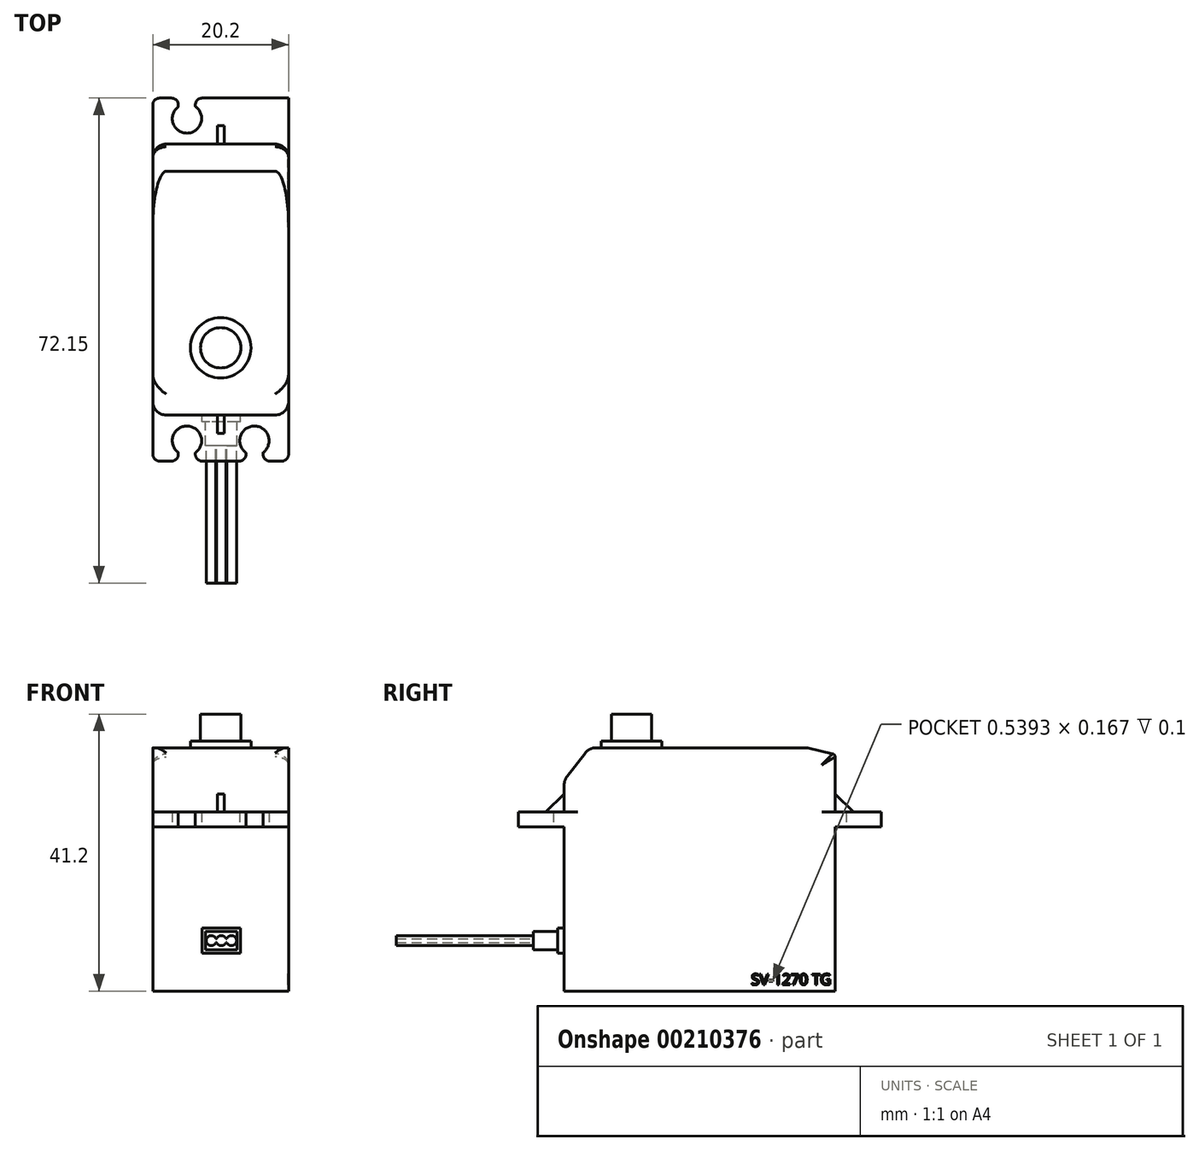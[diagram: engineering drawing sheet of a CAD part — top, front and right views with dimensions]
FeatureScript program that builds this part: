
annotation { "Feature Type Name" : "Feature", "Feature Type Description" : "" }
export const myFeature = defineFeature(function(context is Context, id is Id, definition is map)
    precondition{}
    {
        {
            var Q0;
            Q0=qCreatedBy(makeId("Right.planeOp"),FACE);
            var sketch = newSketch(context, id + "F0", { "sketchPlane" : qUnion([Q0])});
            skLineSegment(sketch, "E0.bottom", {"start": v(-15.65, 18.6) * mm, "end": v(12, 18.6) * mm});
            skLineSegment(sketch, "E0.top", {"start": v(-20.15, -18.6) * mm, "end": v(20.15, -18.6) * mm});
            skLineSegment(sketch, "E0.left", {"start": v(-20.15, 12.78) * mm, "end": v(-20.15, 8.05) * mm});
            skLineSegment(sketch, "E0.right", {"start": v(20.15, 16.61) * mm, "end": v(20.15, 8.05) * mm});
            skPoint(sketch, "E0.middle", {"position": v(0, 0) * mm});
            skLineSegment(sketch, "E1", {"start": v(0, -43.02) * mm, "end": v(0, 43.44) * mm, "construction": true});
            skPoint(sketch, "E1.startSnap0", {"position": v(0, 18.6) * mm});
            skLineSegment(sketch, "E2.0", {"start": v(27, -43.02) * mm, "end": v(27, 43.44) * mm, "construction": true});
            skLineSegment(sketch, "E3.0", {"start": v(-27, -43.02) * mm, "end": v(-27, 43.44) * mm, "construction": true});
            skLineSegment(sketch, "E4", {"start": v(-27, 5.8) * mm, "end": v(27, 5.8) * mm});
            skLineSegment(sketch, "E5.0", {"start": v(-27, 8.05) * mm, "end": v(27, 8.05) * mm});
            skLineSegment(sketch, "E6.0", {"start": v(12, 18.6) * mm, "end": v(12, -18.6) * mm, "construction": true});
            skLineSegment(sketch, "E7.0", {"start": v(-15.65, 18.6) * mm, "end": v(-15.65, -18.6) * mm, "construction": true});
            skLineSegment(sketch, "E8", {"start": v(-15.65, 18.6) * mm, "end": v(-20.15, 12.78) * mm});
            skLineSegment(sketch, "E9", {"start": v(12, 18.6) * mm, "end": v(20.15, 16.61) * mm});
            skPoint(sketch, "E10.orphan", {"position": v(-20.15, 18.6) * mm});
            skPoint(sketch, "E11.orphan", {"position": v(20.15, 18.6) * mm});
            skLineSegment(sketch, "E12", {"start": v(-20.15, 10.7) * mm, "end": v(-22.9, 8.05) * mm});
            skLineSegment(sketch, "E13", {"start": v(-20.15, 10.7) * mm, "end": v(20.15, 10.7) * mm, "construction": true});
            skLineSegment(sketch, "E14.0", {"start": v(22.9, -43.02) * mm, "end": v(22.9, 43.44) * mm, "construction": true});
            skLineSegment(sketch, "E15", {"start": v(20.15, 10.7) * mm, "end": v(22.9, 8.05) * mm});
            skLineSegment(sketch, "E16.trimOffspring", {"start": v(-20.15, 5.8) * mm, "end": v(-20.15, -18.6) * mm});
            skLineSegment(sketch, "E17.trimOffspring", {"start": v(20.15, 5.8) * mm, "end": v(20.15, -18.6) * mm});
            skLineSegment(sketch, "E18", {"start": v(-27, 8.05) * mm, "end": v(-27, 5.8) * mm});
            skLineSegment(sketch, "E19", {"start": v(27, 8.05) * mm, "end": v(27, 5.8) * mm});
            skSolve(sketch);
        }
        {
            var Q0;
            Q0=makeQuery(id+"F0.imprint","IMPRINT",FACE,{"disambiguationData":[TD([[makeQuery(id+"F0.imprint","IMPRINT",EDGE,{"derivedFrom":sQuery(id+"F0.wireOp",EDGE,"E0.top")}),1.0]])]});
            var Q1;
            {var subQ0=sQuery(id+"F0.wireOp",EDGE,"E18");Q1=makeQuery(id+"F0.imprint","IMPRINT",FACE,{"disambiguationData":[TD([[makeQuery(id+"F0.imprint","IMPRINT",EDGE,{"derivedFrom":subQ0}),1.0]])]});}
            var Q2;
            Q2=makeQuery(id+"F0.imprint","IMPRINT",FACE,{"disambiguationData":[TD([[makeQuery(id+"F0.imprint","IMPRINT",EDGE,{"derivedFrom":sQuery(id+"F0.wireOp",EDGE,"E0.bottom")}),-1.0]])]});
            extrude(context, id + "F1", {"entities" : qUnion([Q0, Q1, Q2]), "endBound" : BoundingType.SYMMETRIC, "depth" : 20.2 * mm});
        }
        {
            var Q0;
            {var subQ3=sQuery(id+"F0.wireOp",EDGE,"E12");Q0=makeQuery(id+"F0.imprint","IMPRINT",FACE,{"disambiguationData":[TD([[makeQuery(id+"F0.imprint","IMPRINT",EDGE,{"derivedFrom":subQ3}),1.0]])]});}
            var Q1;
            {var subQ3=sQuery(id+"F0.wireOp",EDGE,"E15");Q1=makeQuery(id+"F0.imprint","IMPRINT",FACE,{"disambiguationData":[TD([[makeQuery(id+"F0.imprint","IMPRINT",EDGE,{"derivedFrom":subQ3}),-1.0]])]});}
            extrude(context, id + "F2", {"entities" : qUnion([Q0, Q1]), "operationType" : NewBodyOperationType.ADD, "endBound" : BoundingType.SYMMETRIC, "depth" : 1 * mm});
        }
        {
            var Q0;
            Q0=makeQuery(id+"F1.opExtrude","SWEPT_FACE",FACE,{"disambiguationData":[OSD([sQuery(id+"F0.wireOp",EDGE,"E0.bottom")])]});
            var sketch = newSketch(context, id + "F3", { "sketchPlane" : qUnion([Q0])});
            skLineSegment(sketch, "E20.0", {"start": v(10.1, -18.65) * mm, "end": v(10.1, 17) * mm});
            skLineSegment(sketch, "E21.0", {"start": v(-10.1, -18.65) * mm, "end": v(-10.1, 17) * mm});
            skLineSegment(sketch, "E22.0", {"start": v(10.1, -14.65) * mm, "end": v(-10.1, -14.65) * mm, "construction": true});
            skLineSegment(sketch, "E23", {"start": v(0, 0) * mm, "end": v(0, -15.65) * mm, "construction": true});
            skCircle(sketch, "E24", {"center": v(0, -10.15) * mm, "radius": 4.5 * mm});
            skCircle(sketch, "E25", {"center": v(0, -10.15) * mm, "radius": 3 * mm});
            skLineSegment(sketch, "E26.0", {"start": v(10.1, -18.65) * mm, "end": v(-10.1, -18.65) * mm});
            skPoint(sketch, "E27.orphan", {"position": v(10.1, -15.65) * mm});
            skPoint(sketch, "E28.orphan", {"position": v(-10.1, -15.65) * mm});
            skLineSegment(sketch, "E29.0", {"start": v(10.1, 17) * mm, "end": v(-10.1, 17) * mm});
            skPoint(sketch, "E30.orphan", {"position": v(10.1, 12) * mm});
            skPoint(sketch, "E31.orphan", {"position": v(-10.1, 12) * mm});
            skSolve(sketch);
        }
        {
            var Q0;
            Q0=makeQuery(id+"F3.imprint","IMPRINT",FACE,{"disambiguationData":[TD([[makeQuery(id+"F3.imprint","IMPRINT",EDGE,{"derivedFrom":sQuery(id+"F3.wireOp",EDGE,"E24")}),-1.0]])]});
            var Q1;
            {var subQ2=sQuery(id+"F3.wireOp",EDGE,"E29.0");Q1=makeQuery(id+"F3.imprint","IMPRINT",FACE,{"disambiguationData":[TD([[makeQuery(id+"F3.imprint","IMPRINT",EDGE,{"derivedFrom":subQ2}),1.0]])]});}
            var Q2;
            {var subQ2=sQuery(id+"F3.wireOp",EDGE,"E26.0");Q2=makeQuery(id+"F3.imprint","IMPRINT",FACE,{"disambiguationData":[TD([[makeQuery(id+"F3.imprint","IMPRINT",EDGE,{"derivedFrom":subQ2}),-1.0]])]});}
            extrude(context, id + "F4", {"entities" : qUnion([Q0, Q1, Q2]), "operationType" : NewBodyOperationType.REMOVE, "oppositeDirection" : true, "depth" : 1 * mm});
        }
        {
            var Q0;
            Q0=makeQuery(id+"F3.imprint","IMPRINT",FACE,{"disambiguationData":[TD([[makeQuery(id+"F3.imprint","IMPRINT",EDGE,{"derivedFrom":sQuery(id+"F3.wireOp",EDGE,"E25")}),1.0]])]});
            extrude(context, id + "F5", {"entities" : qUnion([Q0]), "operationType" : NewBodyOperationType.ADD, "depth" : 4 * mm});
        }
        {
            var Q0;
            Q0=qCreatedBy(makeId("Top.planeOp"),FACE);
            var sketch = newSketch(context, id + "F6", { "sketchPlane" : qUnion([Q0])});
            skLineSegment(sketch, "E32.0", {"start": v(10.1, -24) * mm, "end": v(-10.1, -24) * mm, "construction": true});
            skPoint(sketch, "E33.newPointB", {"position": v(10.1, -27) * mm});
            skLineSegment(sketch, "E34", {"start": v(0, -27.5) * mm, "end": v(0, -27) * mm});
            skLineSegment(sketch, "E35.MirrorCS", {"start": v(3.77, -26) * mm, "end": v(3.77, -25.8) * mm});
            skLineSegment(sketch, "E36.MirrorCS", {"start": v(10.02, -26) * mm, "end": v(10.38, -26) * mm});
            skLineSegment(sketch, "E37.MirrorCS", {"start": v(6.3, -26) * mm, "end": v(6.3, -25.78) * mm});
            skLineSegment(sketch, "E38.MirrorCS", {"start": v(7.3, -27) * mm, "end": v(9.1, -27) * mm});
            skLineSegment(sketch, "E39.MirrorCS", {"start": v(9.1, -27) * mm, "end": v(7.3, -27) * mm});
            skArc(sketch, "E40.MirrorCS", {"start": v(10.1, -26) * mm, "mid": v(9.8, -26.7) * mm, "end": v(9.1, -27) * mm});
            skArc(sketch, "E41.MirrorCS", {"start": v(7.3, -27) * mm, "mid": v(6.6, -26.7) * mm, "end": v(6.3, -26) * mm});
            skLineSegment(sketch, "E42.MirrorCS", {"start": v(10.38, -26) * mm, "end": v(10.38, -27.5) * mm});
            skLineSegment(sketch, "E43.MirrorCS", {"start": v(0, -27) * mm, "end": v(2.77, -27) * mm});
            skArc(sketch, "E44.MirrorCS", {"start": v(3.77, -26) * mm, "mid": v(3.47, -26.7) * mm, "end": v(2.77, -27) * mm});
            skLineSegment(sketch, "E45.MirrorCS", {"start": v(10.38, -27.5) * mm, "end": v(0, -27.5) * mm});
            skPoint(sketch, "E46.MirrorP", {"position": v(3.77, -27) * mm});
            skArc(sketch, "E47", {"start": v(6.34, -25.7) * mm, "mid": v(5, -21.79) * mm, "end": v(3.73, -25.72) * mm});
            skPoint(sketch, "E48.orphan", {"position": v(6.3, -25.52) * mm});
            skPoint(sketch, "E49.orphan", {"position": v(3.77, -25.56) * mm});
            skPoint(sketch, "E50.visualSharp", {"position": v(6.3, -25.73) * mm});
            skArc(sketch, "E50.filletArc", {"start": v(6.34, -25.7) * mm, "mid": v(6.31, -25.73) * mm, "end": v(6.3, -25.78) * mm});
            skPoint(sketch, "E51.visualSharp", {"position": v(3.77, -25.75) * mm});
            skArc(sketch, "E51.filletArc", {"start": v(3.77, -25.8) * mm, "mid": v(3.76, -25.76) * mm, "end": v(3.73, -25.72) * mm});
            skArc(sketch, "E52.MirrorCS", {"start": v(-3.77, -25.8) * mm, "mid": v(-3.76, -25.76) * mm, "end": v(-3.73, -25.72) * mm});
            skLineSegment(sketch, "E53.MirrorCS", {"start": v(-3.77, -26) * mm, "end": v(-3.77, -25.8) * mm});
            skArc(sketch, "E54.MirrorCS", {"start": v(-6.34, -25.7) * mm, "mid": v(-6.31, -25.73) * mm, "end": v(-6.3, -25.78) * mm});
            skLineSegment(sketch, "E55.MirrorCS", {"start": v(-6.3, -26) * mm, "end": v(-6.3, -25.78) * mm});
            skLineSegment(sketch, "E56.MirrorCS", {"start": v(-10.02, -26) * mm, "end": v(-10.38, -26) * mm});
            skLineSegment(sketch, "E57.MirrorCS", {"start": v(-10.38, -26) * mm, "end": v(-10.38, -27.5) * mm});
            skLineSegment(sketch, "E58.MirrorCS", {"start": v(-9.1, -27) * mm, "end": v(-7.3, -27) * mm});
            skArc(sketch, "E59.MirrorCS", {"start": v(-10.1, -26) * mm, "mid": v(-9.8, -26.7) * mm, "end": v(-9.1, -27) * mm});
            skPoint(sketch, "E60.MirrorP", {"position": v(-10.1, -27) * mm});
            skArc(sketch, "E61.MirrorCS", {"start": v(-3.77, -26) * mm, "mid": v(-3.47, -26.7) * mm, "end": v(-2.77, -27) * mm});
            skLineSegment(sketch, "E62.MirrorCS", {"start": v(-7.3, -27) * mm, "end": v(-9.1, -27) * mm});
            skLineSegment(sketch, "E63.MirrorCS", {"start": v(0, -27) * mm, "end": v(-2.77, -27) * mm});
            skArc(sketch, "E64.MirrorCS", {"start": v(-7.3, -27) * mm, "mid": v(-6.6, -26.7) * mm, "end": v(-6.3, -26) * mm});
            skPoint(sketch, "E65.MirrorP", {"position": v(-3.77, -25.75) * mm});
            skPoint(sketch, "E66.MirrorP", {"position": v(-3.77, -25.56) * mm});
            skPoint(sketch, "E67.MirrorP", {"position": v(-3.77, -27) * mm});
            skLineSegment(sketch, "E68.MirrorCS", {"start": v(-10.38, -27.5) * mm, "end": v(0, -27.5) * mm});
            skArc(sketch, "E69.MirrorCS", {"start": v(-6.34, -25.7) * mm, "mid": v(-5, -21.79) * mm, "end": v(-3.73, -25.72) * mm});
            skPoint(sketch, "E70.MirrorP", {"position": v(-6.3, -25.73) * mm});
            skPoint(sketch, "E71.MirrorP", {"position": v(-6.3, -25.52) * mm});
            skLineSegment(sketch, "E72.MirrorCS", {"start": v(-10.1, -24) * mm, "end": v(10.1, -24) * mm, "construction": true});
            skLineSegment(sketch, "E73.MirrorCS", {"start": v(0, 27.5) * mm, "end": v(0, 27) * mm});
            skArc(sketch, "E74.MirrorCS", {"start": v(-3.77, 25.8) * mm, "mid": v(-3.76, 25.76) * mm, "end": v(-3.73, 25.72) * mm});
            skLineSegment(sketch, "E75.MirrorCS", {"start": v(-3.77, 26) * mm, "end": v(-3.77, 25.8) * mm});
            skArc(sketch, "E76.MirrorCS", {"start": v(3.77, 25.8) * mm, "mid": v(3.76, 25.76) * mm, "end": v(3.73, 25.72) * mm});
            skLineSegment(sketch, "E77.MirrorCS", {"start": v(3.77, 26) * mm, "end": v(3.77, 25.8) * mm});
            skLineSegment(sketch, "E78.MirrorCS", {"start": v(6.3, 26) * mm, "end": v(6.3, 25.78) * mm});
            skArc(sketch, "E79.MirrorCS", {"start": v(6.34, 25.7) * mm, "mid": v(6.31, 25.73) * mm, "end": v(6.3, 25.78) * mm});
            skArc(sketch, "E80.MirrorCS", {"start": v(-6.34, 25.7) * mm, "mid": v(-6.31, 25.73) * mm, "end": v(-6.3, 25.78) * mm});
            skLineSegment(sketch, "E81.MirrorCS", {"start": v(-6.3, 26) * mm, "end": v(-6.3, 25.78) * mm});
            skArc(sketch, "E82.MirrorCS", {"start": v(-10.1, 26) * mm, "mid": v(-9.8, 26.7) * mm, "end": v(-9.1, 27) * mm});
            skLineSegment(sketch, "E83.MirrorCS", {"start": v(7.3, 27) * mm, "end": v(9.1, 27) * mm});
            skLineSegment(sketch, "E84.MirrorCS", {"start": v(-7.3, 27) * mm, "end": v(-9.1, 27) * mm});
            skLineSegment(sketch, "E85.MirrorCS", {"start": v(-10.38, 26) * mm, "end": v(-10.38, 27.5) * mm});
            skLineSegment(sketch, "E86.MirrorCS", {"start": v(10.38, 26) * mm, "end": v(10.38, 27.5) * mm});
            skLineSegment(sketch, "E87.MirrorCS", {"start": v(10.02, 26) * mm, "end": v(10.38, 26) * mm});
            skLineSegment(sketch, "E88.MirrorCS", {"start": v(-10.02, 26) * mm, "end": v(-10.38, 26) * mm});
            skArc(sketch, "E89.MirrorCS", {"start": v(10.1, 26) * mm, "mid": v(9.8, 26.7) * mm, "end": v(9.1, 27) * mm});
            skLineSegment(sketch, "E90.MirrorCS", {"start": v(-9.1, 27) * mm, "end": v(-7.3, 27) * mm});
            skLineSegment(sketch, "E91.MirrorCS", {"start": v(9.1, 27) * mm, "end": v(7.3, 27) * mm});
            skPoint(sketch, "E92.MirrorP", {"position": v(3.77, 25.75) * mm});
            skPoint(sketch, "E93.MirrorP", {"position": v(10.1, 27) * mm});
            skArc(sketch, "E94.MirrorCS", {"start": v(-3.77, 26) * mm, "mid": v(-3.47, 26.7) * mm, "end": v(-2.77, 27) * mm});
            skPoint(sketch, "E95.MirrorP", {"position": v(-10.1, 27) * mm});
            skArc(sketch, "E96.MirrorCS", {"start": v(3.77, 26) * mm, "mid": v(3.47, 26.7) * mm, "end": v(2.77, 27) * mm});
            skPoint(sketch, "E97.MirrorP", {"position": v(6.3, 25.73) * mm});
            skPoint(sketch, "E98.MirrorP", {"position": v(-3.77, 25.75) * mm});
            skPoint(sketch, "E99.MirrorP", {"position": v(6.3, 25.52) * mm});
            skLineSegment(sketch, "E100.MirrorCS", {"start": v(10.1, 24) * mm, "end": v(-10.1, 24) * mm, "construction": true});
            skLineSegment(sketch, "E101.MirrorCS", {"start": v(-10.1, 24) * mm, "end": v(10.1, 24) * mm, "construction": true});
            skPoint(sketch, "E102.MirrorP", {"position": v(-3.77, 25.56) * mm});
            skPoint(sketch, "E103.MirrorP", {"position": v(3.77, 25.56) * mm});
            skPoint(sketch, "E104.MirrorP", {"position": v(-6.3, 25.73) * mm});
            skLineSegment(sketch, "E105.MirrorCS", {"start": v(0, 27) * mm, "end": v(2.77, 27) * mm});
            skPoint(sketch, "E106.MirrorP", {"position": v(-6.3, 25.52) * mm});
            skPoint(sketch, "E107.MirrorP", {"position": v(-3.77, 27) * mm});
            skArc(sketch, "E108.MirrorCS", {"start": v(6.34, 25.7) * mm, "mid": v(5, 21.79) * mm, "end": v(3.73, 25.72) * mm});
            skPoint(sketch, "E109.MirrorP", {"position": v(3.77, 27) * mm});
            skLineSegment(sketch, "E110.MirrorCS", {"start": v(0, 27) * mm, "end": v(-2.77, 27) * mm});
            skArc(sketch, "E111.MirrorCS", {"start": v(-6.34, 25.7) * mm, "mid": v(-5, 21.79) * mm, "end": v(-3.73, 25.72) * mm});
            skLineSegment(sketch, "E112.MirrorCS", {"start": v(10.38, 27.5) * mm, "end": v(0, 27.5) * mm});
            skArc(sketch, "E113.MirrorCS", {"start": v(7.3, 27) * mm, "mid": v(6.6, 26.7) * mm, "end": v(6.3, 26) * mm});
            skArc(sketch, "E114.MirrorCS", {"start": v(-7.3, 27) * mm, "mid": v(-6.6, 26.7) * mm, "end": v(-6.3, 26) * mm});
            skLineSegment(sketch, "E115.MirrorCS", {"start": v(-10.38, 27.5) * mm, "end": v(0, 27.5) * mm});
            skSolve(sketch);
        }
        {
            var Q0;
            Q0=makeQuery(id+"F6.imprint","IMPRINT",FACE,{"disambiguationData":[TD([[makeQuery(id+"F6.imprint","IMPRINT",EDGE,{"derivedFrom":sQuery(id+"F6.wireOp",EDGE,"E35.MirrorCS")}),-1.0]])]});
            var Q1;
            Q1=makeQuery(id+"F6.imprint","IMPRINT",FACE,{"disambiguationData":[TD([[makeQuery(id+"F6.imprint","IMPRINT",EDGE,{"derivedFrom":sQuery(id+"F6.wireOp",EDGE,"E55.MirrorCS")}),-1.0]])]});
            var Q2;
            Q2=makeQuery(id+"F6.imprint","IMPRINT",FACE,{"disambiguationData":[TD([[makeQuery(id+"F6.imprint","IMPRINT",EDGE,{"derivedFrom":sQuery(id+"F6.wireOp",EDGE,"E76.MirrorCS")}),1.0]])]});
            var Q3;
            Q3=makeQuery(id+"F6.imprint","IMPRINT",FACE,{"disambiguationData":[TD([[makeQuery(id+"F6.imprint","IMPRINT",EDGE,{"derivedFrom":sQuery(id+"F6.wireOp",EDGE,"E74.MirrorCS")}),-1.0]])]});
            extrude(context, id + "F7", {"entities" : qUnion([Q0, Q1, Q2, Q3]), "operationType" : NewBodyOperationType.REMOVE, "depth" : 25 * mm});
        }
        {
            var Q0;
            Q0=makeQuery(id+"F1.opExtrude","CAP_EDGE",EDGE,{"disambiguationData":[OSD([sQuery(id+"F0.wireOp",EDGE,"E0.right")])],"isStart":true});
            var Q1;
            Q1=makeQuery(id+"F1.opExtrude","CAP_EDGE",EDGE,{"disambiguationData":[OSD([sQuery(id+"F0.wireOp",EDGE,"E9")])],"isStart":true});
            var Q2;
            Q2=makeQuery(id+"F4.boolean.opBoolean","COPY",EDGE,{"derivedFrom":makeQuery(id+"F4.opExtrude","CAP_EDGE",EDGE,{"disambiguationData":[OSD([sQuery(id+"F3.wireOp",EDGE,"E21.0")])],"isStart":false})});
            var Q3;
            Q3=makeQuery(id+"F1.opExtrude","CAP_EDGE",EDGE,{"disambiguationData":[OSD([sQuery(id+"F0.wireOp",EDGE,"E8")])],"isStart":true});
            var Q4;
            Q4=makeQuery(id+"F1.opExtrude","CAP_EDGE",EDGE,{"disambiguationData":[OSD([sQuery(id+"F0.wireOp",EDGE,"E0.left")])],"isStart":true});
            var Q5;
            Q5=makeQuery(id+"F1.opExtrude","CAP_EDGE",EDGE,{"disambiguationData":[OSD([sQuery(id+"F0.wireOp",EDGE,"E0.right")])],"isStart":false});
            var Q6;
            Q6=makeQuery(id+"F1.opExtrude","CAP_EDGE",EDGE,{"disambiguationData":[OSD([sQuery(id+"F0.wireOp",EDGE,"E9")])],"isStart":false});
            var Q7;
            Q7=makeQuery(id+"F4.boolean.opBoolean","COPY",EDGE,{"derivedFrom":makeQuery(id+"F4.opExtrude","CAP_EDGE",EDGE,{"disambiguationData":[OSD([sQuery(id+"F3.wireOp",EDGE,"E20.0")])],"isStart":false})});
            var Q8;
            Q8=makeQuery(id+"F1.opExtrude","SWEPT_EDGE",EDGE,{"disambiguationData":[OSD([sQuery(id+"F0.wireOp",EDGE,"E0.left"),sQuery(id+"F0.wireOp",EDGE,"E8")])]});
            var Q9;
            Q9=makeQuery(id+"F4.boolean.opBoolean","INTERSECT",EDGE,{"derivedFrom":[makeQuery(id+"F1.opExtrude","SWEPT_FACE",FACE,{"disambiguationData":[OSD([sQuery(id+"F0.wireOp",EDGE,"E8")])]}),makeQuery(id+"F4.opExtrude","CAP_FACE",FACE,{"disambiguationData":[OSD([sQuery(id+"F3.wireOp",EDGE,"E20.0"),sQuery(id+"F3.wireOp",EDGE,"E21.0"),sQuery(id+"F3.wireOp",EDGE,"E24"),sQuery(id+"F3.wireOp",EDGE,"E26.0"),sQuery(id+"F3.wireOp",EDGE,"E29.0")])],"isStart":false})]});
            var Q10;
            Q10=makeQuery(id+"F1.opExtrude","CAP_EDGE",EDGE,{"disambiguationData":[OSD([sQuery(id+"F0.wireOp",EDGE,"E0.left")])],"isStart":false});
            var Q11;
            Q11=makeQuery(id+"F1.opExtrude","CAP_EDGE",EDGE,{"disambiguationData":[OSD([sQuery(id+"F0.wireOp",EDGE,"E8")])],"isStart":false});
            fillet(context, id + "F8", {"entities" : qUnion([Q0, Q1, Q2, Q3, Q4, Q5, Q6, Q7, Q8, Q9, Q10, Q11]), "radius" : 2 * mm, "tangentPropagation" : true, "allowEdgeOverflow" : false});
        }
        {
            var Q0;
            Q0=makeQuery(id+"F1.opExtrude","SWEPT_FACE",FACE,{"disambiguationData":[OSD([sQuery(id+"F0.wireOp",EDGE,"E16.trimOffspring")])]});
            var sketch = newSketch(context, id + "F9", { "sketchPlane" : qUnion([Q0])});
            skLineSegment(sketch, "E116.0", {"start": v(2.97, -12.95) * mm, "end": v(-2.77, -12.95) * mm});
            skLineSegment(sketch, "E117.0", {"start": v(2.97, -9.25) * mm, "end": v(-2.77, -9.25) * mm});
            skLineSegment(sketch, "E118", {"start": v(2.97, -9.25) * mm, "end": v(2.97, -12.95) * mm});
            skLineSegment(sketch, "E119", {"start": v(-2.77, -9.25) * mm, "end": v(-2.77, -12.95) * mm});
            skLineSegment(sketch, "E120.0", {"start": v(2.47, -9.75) * mm, "end": v(-2.27, -9.75) * mm});
            skLineSegment(sketch, "E120.1", {"start": v(2.47, -9.75) * mm, "end": v(2.47, -12.45) * mm});
            skLineSegment(sketch, "E120.2", {"start": v(2.47, -12.45) * mm, "end": v(-2.27, -12.45) * mm});
            skLineSegment(sketch, "E120.3", {"start": v(-2.27, -9.75) * mm, "end": v(-2.27, -12.45) * mm});
            skLineSegment(sketch, "E121", {"start": v(2.47, -11.1) * mm, "end": v(-2.27, -11.1) * mm, "construction": true});
            skArc(sketch, "E122", {"start": v(-0.59, -11.4) * mm, "mid": v(0.1, -11.85) * mm, "end": v(0.79, -11.4) * mm});
            skArc(sketch, "E123", {"start": v(-0.71, -10.8) * mm, "mid": v(-2.15, -11.1) * mm, "end": v(-0.71, -11.4) * mm});
            skArc(sketch, "E124", {"start": v(0.91, -11.4) * mm, "mid": v(2.35, -11.1) * mm, "end": v(0.91, -10.8) * mm});
            skLineSegment(sketch, "E125.trimOffspring", {"start": v(-0.59, -10.8) * mm, "end": v(-0.71, -10.8) * mm});
            skLineSegment(sketch, "E126.trimOffspring", {"start": v(-0.59, -11.4) * mm, "end": v(-0.71, -11.4) * mm});
            skArc(sketch, "E127.trimOffspring", {"start": v(0.79, -10.8) * mm, "mid": v(0.1, -10.35) * mm, "end": v(-0.59, -10.8) * mm});
            skLineSegment(sketch, "E128.trimOffspring", {"start": v(0.91, -10.8) * mm, "end": v(0.79, -10.8) * mm});
            skLineSegment(sketch, "E129.trimOffspring", {"start": v(0.91, -11.4) * mm, "end": v(0.79, -11.4) * mm});
            skSolve(sketch);
        }
        {
            var Q0;
            Q0=makeQuery(id+"F9.imprint","IMPRINT",FACE,{"disambiguationData":[TD([[makeQuery(id+"F9.imprint","IMPRINT",EDGE,{"derivedFrom":sQuery(id+"F9.wireOp",EDGE,"E116.0")}),-1.0]])]});
            extrude(context, id + "F10", {"entities" : qUnion([Q0]), "operationType" : NewBodyOperationType.ADD, "depth" : 1 * mm});
        }
        {
            var Q0;
            Q0=makeQuery(id+"F9.imprint","IMPRINT",FACE,{"disambiguationData":[TD([[makeQuery(id+"F9.imprint","IMPRINT",EDGE,{"derivedFrom":sQuery(id+"F9.wireOp",EDGE,"E120.0")}),1.0]])]});
            extrude(context, id + "F11", {"entities" : qUnion([Q0]), "operationType" : NewBodyOperationType.ADD, "depth" : 4.57 * mm});
        }
        {
            var Q0;
            Q0=makeQuery(id+"F9.imprint","IMPRINT",FACE,{"disambiguationData":[TD([[makeQuery(id+"F9.imprint","IMPRINT",EDGE,{"derivedFrom":sQuery(id+"F9.wireOp",EDGE,"E122")}),1.0]])]});
            extrude(context, id + "F12", {"entities" : qUnion([Q0]), "operationType" : NewBodyOperationType.ADD, "depth" : 25 * mm});
        }
        {
            var Q0;
            Q0=makeQuery(id+"F1.opExtrude","CAP_FACE",FACE,{"disambiguationData":[OSD([sQuery(id+"F0.wireOp",EDGE,"E0.bottom"),sQuery(id+"F0.wireOp",EDGE,"E0.top"),sQuery(id+"F0.wireOp",EDGE,"E0.left"),sQuery(id+"F0.wireOp",EDGE,"E0.right"),sQuery(id+"F0.wireOp",EDGE,"E4"),sQuery(id+"F0.wireOp",EDGE,"E5.0"),sQuery(id+"F0.wireOp",EDGE,"E8"),sQuery(id+"F0.wireOp",EDGE,"E9"),sQuery(id+"F0.wireOp",EDGE,"E16.trimOffspring"),sQuery(id+"F0.wireOp",EDGE,"E17.trimOffspring"),sQuery(id+"F0.wireOp",EDGE,"E18"),sQuery(id+"F0.wireOp",EDGE,"E19")])],"isStart":false});
            var sketch = newSketch(context, id + "F13", { "sketchPlane" : qUnion([Q0])});
            skText(sketch, "E130", { "text": "SV-1270 TG", "fontName": "OpenSans-Regular.ttf"});
            const initialGuessF13  = {"E130": [0.00766, -0.01767, 1, 0, 0.00162]};
            skSetInitialGuess(sketch, initialGuessF13);
            skSolve(sketch);
        }
        {
            var Q0;
            Q0 = qSketchRegion(id + "F13", true);
            extrude(context, id + "F14", {"entities" : qUnion([Q0]), "operationType" : NewBodyOperationType.REMOVE, "oppositeDirection" : true, "depth" : 0.1 * mm});
        }
        {
            var Q0;
            Q0=makeQuery(id+"F1.opExtrude","SWEPT_EDGE",EDGE,{"disambiguationData":[OSD([sQuery(id+"F0.wireOp",EDGE,"E0.right"),sQuery(id+"F0.wireOp",EDGE,"E9")])]});
            fillet(context, id + "F15", {"entities" : qUnion([Q0]), "radius" : 0.5 * mm, "tangentPropagation" : true, "allowEdgeOverflow" : false});
        }
    });
